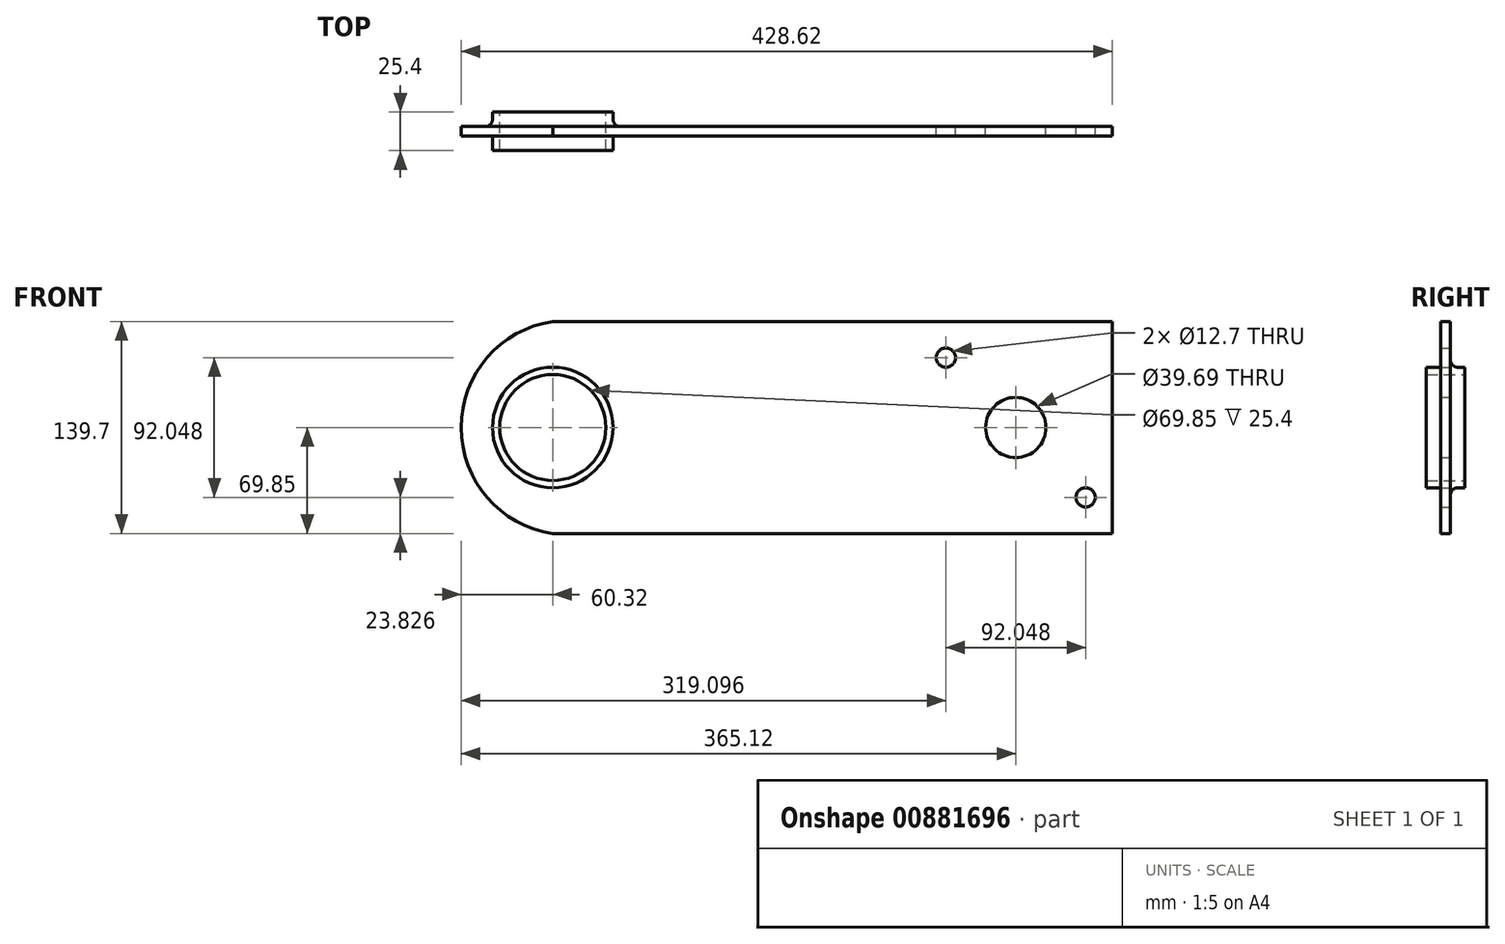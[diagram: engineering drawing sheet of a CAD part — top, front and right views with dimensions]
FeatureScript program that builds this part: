
annotation { "Feature Type Name" : "Feature", "Feature Type Description" : "" }
export const myFeature = defineFeature(function(context is Context, id is Id, definition is map)
    precondition{}
    {
        {
            var Q0;
            Q0=qCreatedBy(makeId("Front.planeOp"),FACE);
            var sketch = newSketch(context, id + "F0", { "sketchPlane" : qUnion([Q0])});
            skLineSegment(sketch, "E0.bottom", {"start": v(215.9, 69.85) * mm, "end": v(-152.4, 69.85) * mm});
            skLineSegment(sketch, "E0.top", {"start": v(215.9, -69.85) * mm, "end": v(-152.4, -69.85) * mm});
            skLineSegment(sketch, "E0.left", {"start": v(215.9, 69.85) * mm, "end": v(215.9, -69.85) * mm});
            skPoint(sketch, "E0.middle", {"position": v(0, 0) * mm});
            skCircle(sketch, "E1", {"center": v(152.4, 0) * mm, "radius": 19.84 * mm});
            skCircle(sketch, "E2", {"center": v(-152.4, 0) * mm, "radius": 39.69 * mm});
            skCircle(sketch, "E3", {"center": v(-152.4, 0) * mm, "radius": 34.93 * mm});
            skPoint(sketch, "E4", {"position": v(-212.72, 0) * mm});
            skArc(sketch, "E5", {"start": v(-152.4, 69.85) * mm, "mid": v(-212.72, 0) * mm, "end": v(-152.4, -69.85) * mm});
            skPoint(sketch, "E0.right.end.orphan", {"position": v(-215.9, -69.85) * mm});
            skPoint(sketch, "E0.right.start.orphan", {"position": v(-215.9, 69.85) * mm});
            skSolve(sketch);
        }
        {
            var Q0;
            Q0=makeQuery(id+"F0.imprint","IMPRINT",FACE,{"disambiguationData":[TD([[makeQuery(id+"F0.imprint","IMPRINT",EDGE,{"derivedFrom":sQuery(id+"F0.wireOp",EDGE,"E0.bottom")}),1.0]])]});
            extrude(context, id + "F1", {"entities" : qUnion([Q0]), "endBound" : BoundingType.SYMMETRIC, "depth" : 6.35 * mm, "offsetDistance" : 25.4 * mm});
        }
        {
            var Q0;
            Q0=makeQuery(id+"F0.imprint","IMPRINT",FACE,{"disambiguationData":[TD([[makeQuery(id+"F0.imprint","IMPRINT",EDGE,{"derivedFrom":sQuery(id+"F0.wireOp",EDGE,"E2")}),1.0]])]});
            extrude(context, id + "F2", {"entities" : qUnion([Q0]), "operationType" : NewBodyOperationType.ADD, "endBound" : BoundingType.SYMMETRIC, "depth" : 25.4 * mm, "offsetDistance" : 25.4 * mm});
        }
        {
            var Q0;
            Q0=makeQuery(id+"F1.opExtrude","CAP_EDGE",EDGE,{"disambiguationData":[OSD([sQuery(id+"F0.wireOp",EDGE,"E2")])],"isStart":false});
            var Q1;
            Q1=makeQuery(id+"F1.opExtrude","CAP_EDGE",EDGE,{"disambiguationData":[OSD([sQuery(id+"F0.wireOp",EDGE,"E2")])],"isStart":true});
            fillet(context, id + "F3", {"entities" : qUnion([Q0, Q1]), "radius" : 4.76 * mm, "tangentPropagation" : true, "allowEdgeOverflow" : false});
        }
        {
            var Q0;
            Q0=makeQuery(id+"F1.opExtrude","CAP_FACE",FACE,{"disambiguationData":[OSD([sQuery(id+"F0.wireOp",EDGE,"E0.bottom"),sQuery(id+"F0.wireOp",EDGE,"E0.top"),sQuery(id+"F0.wireOp",EDGE,"E0.left"),sQuery(id+"F0.wireOp",EDGE,"E1"),sQuery(id+"F0.wireOp",EDGE,"E2"),sQuery(id+"F0.wireOp",EDGE,"E5")])],"isStart":true});
            var sketch = newSketch(context, id + "F4", { "sketchPlane" : qUnion([Q0])});
            skCircle(sketch, "E6", {"center": v(-106.38, 46.02) * mm, "radius": 6.75 * mm});
            skCircle(sketch, "E7", {"center": v(-198.42, -46.02) * mm, "radius": 6.75 * mm});
            skSolve(sketch);
        }
        {
            var Q0;
            Q0=sQuery(id+"F4.wireOp",VERTEX,"E6.center");
            var Q1;
            Q1=sQuery(id+"F4.wireOp",VERTEX,"E7.center");
            var Q2;
            Q2=makeQuery(id+"F1.opExtrude","SWEPT_BODY",BODY,{"disambiguationData":[OSD([sQuery(id+"F0.wireOp",EDGE,"E0.bottom"),sQuery(id+"F0.wireOp",EDGE,"E0.top"),sQuery(id+"F0.wireOp",EDGE,"E0.left"),sQuery(id+"F0.wireOp",EDGE,"E1"),sQuery(id+"F0.wireOp",EDGE,"E2"),sQuery(id+"F0.wireOp",EDGE,"E5")])]});
            hole(context, id + "F5", {"style" : HoleStyle.SIMPLE, "endStyle" : HoleEndStyle.THROUGH, "holeDiameter" : 12.7 * mm, "majorDiameter" : 6.35 * mm, "isTappedThrough" : true, "tappedDepth" : 12.7 * mm, "tapClearance" : 3, "locations" : qUnion([Q0, Q1]), "scope" : qUnion([Q2])});
        }
    });
